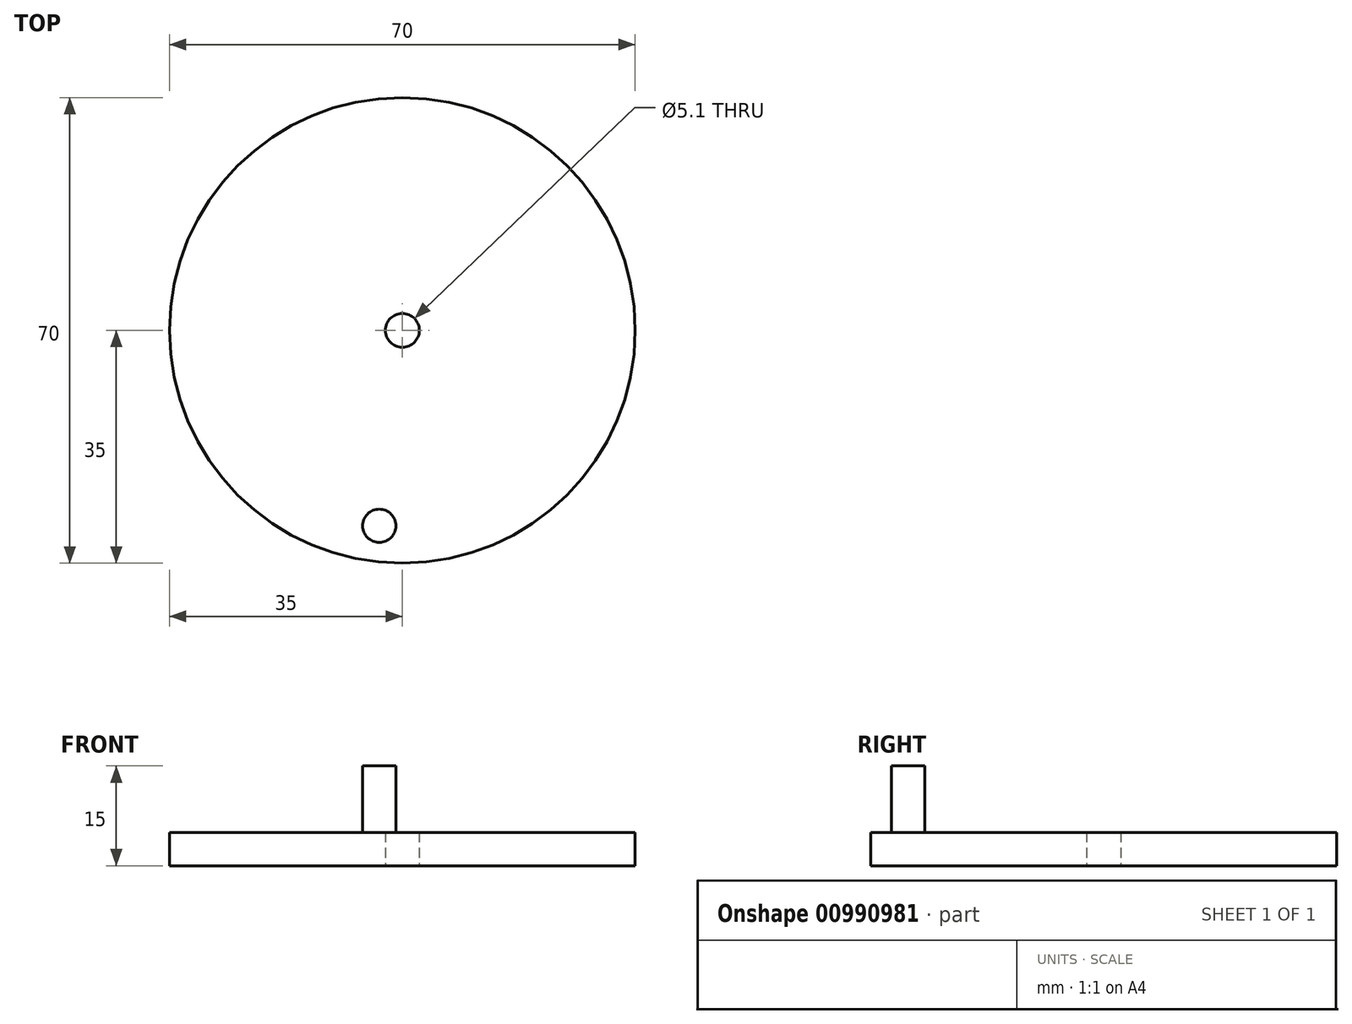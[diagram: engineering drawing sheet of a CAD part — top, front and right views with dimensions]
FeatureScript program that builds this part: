
annotation { "Feature Type Name" : "Feature", "Feature Type Description" : "" }
export const myFeature = defineFeature(function(context is Context, id is Id, definition is map)
    precondition{}
    {
        {
            var Q0;
            Q0=qCreatedBy(makeId("Top.planeOp"),FACE);
            var sketch = newSketch(context, id + "F0", { "sketchPlane" : qUnion([Q0])});
            skCircle(sketch, "E0", {"center": v(0, 0) * mm, "radius": 35 * mm});
            skCircle(sketch, "E1", {"center": v(0, 0) * mm, "radius": 2.55 * mm});
            skSolve(sketch);
        }
        {
            var Q0;
            Q0=makeQuery(id+"F0.imprint","IMPRINT",FACE,{"disambiguationData":[TD([[makeQuery(id+"F0.imprint","IMPRINT",EDGE,{"derivedFrom":sQuery(id+"F0.wireOp",EDGE,"E0")}),1.0]])]});
            extrude(context, id + "F1", {"entities" : qUnion([Q0]), "depth" : 5 * mm, "offsetDistance" : 25 * mm});
        }
        {
            var Q0;
            Q0=makeQuery(id+"F1.opExtrude","CAP_FACE",FACE,{"disambiguationData":[OSD([sQuery(id+"F0.wireOp",EDGE,"E0"),sQuery(id+"F0.wireOp",EDGE,"E1")])],"isStart":false});
            var sketch = newSketch(context, id + "F2", { "sketchPlane" : qUnion([Q0])});
            skCircle(sketch, "E2", {"center": v(-3.47, -29.39) * mm, "radius": 2.5 * mm});
            skSolve(sketch);
        }
        {
            var Q0;
            Q0=makeQuery(id+"F2.imprint","IMPRINT",FACE,{"disambiguationData":[TD([[makeQuery(id+"F2.imprint","IMPRINT",EDGE,{"derivedFrom":sQuery(id+"F2.wireOp",EDGE,"f7556602-a624-47a5-a552-35f99dc2bc6d")}),1.0]])]});
            var Q1;
            Q1=makeQuery(id+"F2.imprint","IMPRINT",FACE,{"disambiguationData":[TD([[makeQuery(id+"F2.imprint","IMPRINT",EDGE,{"derivedFrom":sQuery(id+"F2.wireOp",EDGE,"E2")}),1.0]])]});
            extrude(context, id + "F3", {"entities" : qUnion([Q0, Q1]), "operationType" : NewBodyOperationType.ADD, "depth" : 10 * mm, "offsetDistance" : 25 * mm});
        }
    });
